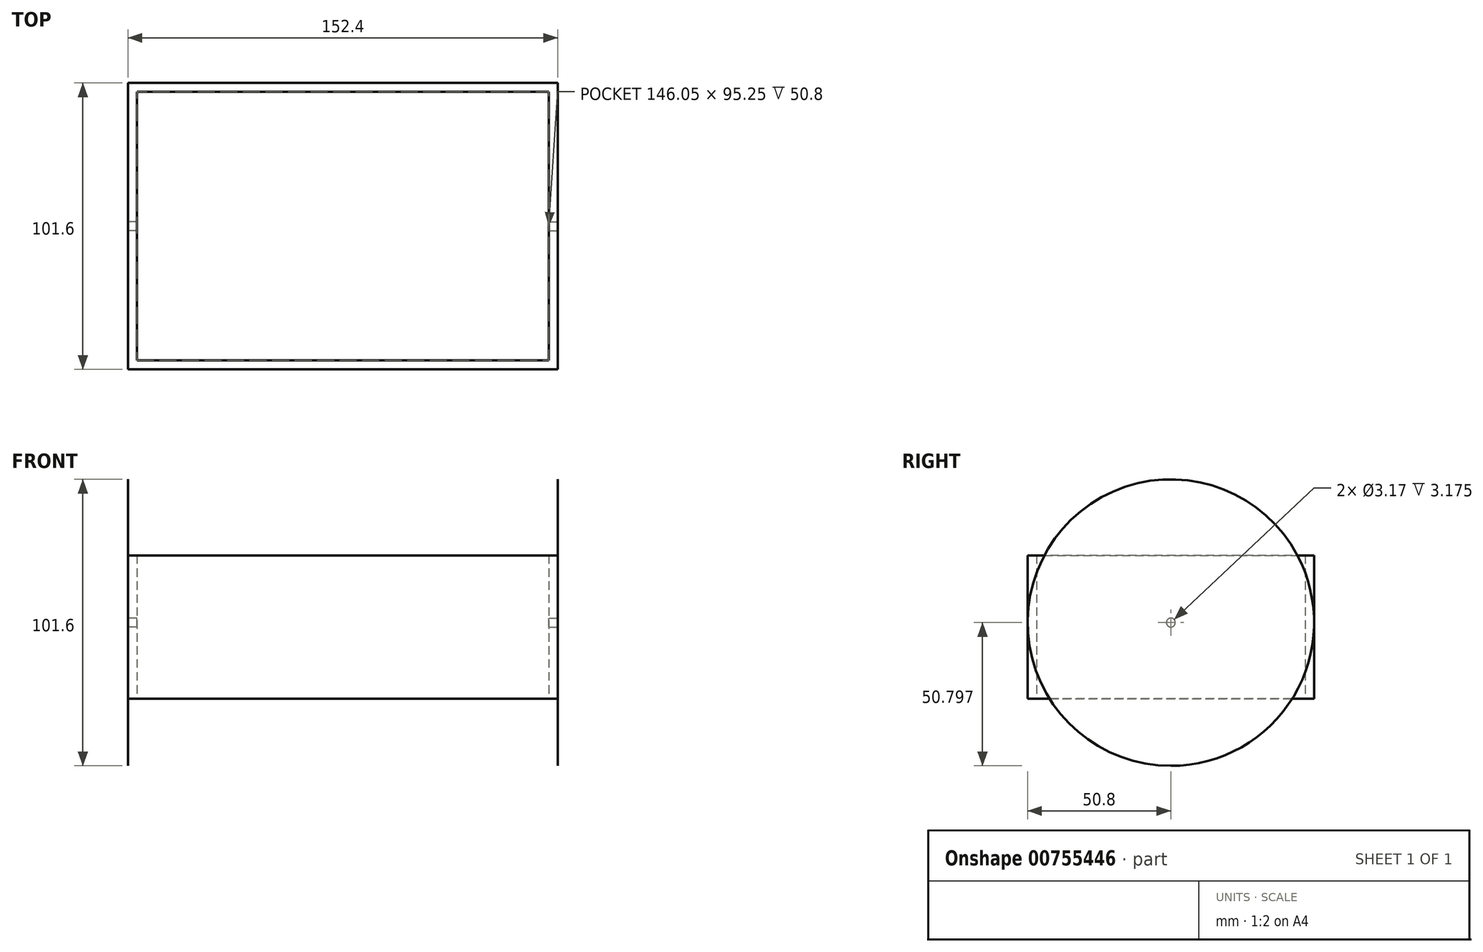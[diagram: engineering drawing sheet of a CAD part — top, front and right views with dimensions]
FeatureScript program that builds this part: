
annotation { "Feature Type Name" : "Feature", "Feature Type Description" : "" }
export const myFeature = defineFeature(function(context is Context, id is Id, definition is map)
    precondition{}
    {
        {
            var Q0;
            Q0=qCreatedBy(makeId("Top.planeOp"),FACE);
            var sketch = newSketch(context, id + "F0", { "sketchPlane" : qUnion([Q0])});
            skLineSegment(sketch, "E0.bottom", {"start": v(76.2, -50.8) * mm, "end": v(-76.2, -50.8) * mm});
            skLineSegment(sketch, "E0.top", {"start": v(76.2, 50.8) * mm, "end": v(-76.2, 50.8) * mm});
            skLineSegment(sketch, "E0.left", {"start": v(76.2, -50.8) * mm, "end": v(76.2, 50.8) * mm});
            skLineSegment(sketch, "E0.right", {"start": v(-76.2, -50.8) * mm, "end": v(-76.2, 50.8) * mm});
            skPoint(sketch, "E0.middle", {"position": v(0, 0) * mm});
            skSolve(sketch);
        }
        {
            var Q0;
            Q0 = qSketchRegion(id + "F0", true);
            extrude(context, id + "F1", {"entities" : qUnion([Q0]), "depth" : 1 / 203.2 * mm, "offsetDistance" : 25.4 * mm});
        }
        {
            var Q0;
            Q0=makeQuery(id+"F1.opExtrude","CAP_FACE",FACE,{"disambiguationData":[OSD([sQuery(id+"F0.wireOp",EDGE,"E0.bottom"),sQuery(id+"F0.wireOp",EDGE,"E0.top"),sQuery(id+"F0.wireOp",EDGE,"E0.left"),sQuery(id+"F0.wireOp",EDGE,"E0.right")])],"isStart":false});
            var sketch = newSketch(context, id + "F2", { "sketchPlane" : qUnion([Q0])});
            skLineSegment(sketch, "E1.bottom", {"start": v(-76.2, 50.8) * mm, "end": v(-73.03, 50.8) * mm});
            skLineSegment(sketch, "E1.top", {"start": v(-76.2, -50.8) * mm, "end": v(-73.03, -50.8) * mm});
            skLineSegment(sketch, "E1.left", {"start": v(-76.2, 50.8) * mm, "end": v(-76.2, -50.8) * mm});
            skLineSegment(sketch, "E1.right", {"start": v(-73.03, 50.8) * mm, "end": v(-73.03, -50.8) * mm});
            skLineSegment(sketch, "E2.bottom", {"start": v(76.2, 50.8) * mm, "end": v(73.02, 50.8) * mm});
            skLineSegment(sketch, "E2.top", {"start": v(76.2, -50.8) * mm, "end": v(73.03, -50.8) * mm});
            skLineSegment(sketch, "E2.left", {"start": v(76.2, 50.8) * mm, "end": v(76.2, -50.8) * mm});
            skLineSegment(sketch, "E2.right", {"start": v(73.02, 50.8) * mm, "end": v(73.03, -50.8) * mm});
            skLineSegment(sketch, "E3.bottom", {"start": v(-73.03, 50.8) * mm, "end": v(73.03, 50.8) * mm});
            skLineSegment(sketch, "E3.top", {"start": v(-73.03, 47.63) * mm, "end": v(73.03, 47.63) * mm});
            skLineSegment(sketch, "E3.left", {"start": v(-73.03, 50.8) * mm, "end": v(-73.03, 47.63) * mm});
            skLineSegment(sketch, "E3.right", {"start": v(73.03, 50.8) * mm, "end": v(73.03, 47.63) * mm});
            skLineSegment(sketch, "E4.bottom", {"start": v(-73.03, -50.8) * mm, "end": v(73.03, -50.8) * mm});
            skLineSegment(sketch, "E4.top", {"start": v(-73.03, -47.63) * mm, "end": v(73.03, -47.63) * mm});
            skLineSegment(sketch, "E4.left", {"start": v(-73.03, -50.8) * mm, "end": v(-73.03, -47.63) * mm});
            skLineSegment(sketch, "E4.right", {"start": v(73.03, -50.8) * mm, "end": v(73.03, -47.63) * mm});
            skSolve(sketch);
        }
        {
            var Q0;
            Q0 = qSketchRegion(id + "F2", true);
            extrude(context, id + "F3", {"entities" : qUnion([Q0]), "operationType" : NewBodyOperationType.ADD, "depth" : 50.8 * mm, "offsetDistance" : 25.4 * mm});
        }
        {
            var Q0;
            Q0=makeQuery(id+"F3.boolean.opBoolean","MERGE",FACE,{"derivedFrom":[makeQuery(id+"F1.opExtrude","SWEPT_FACE",FACE,{"disambiguationData":[OSD([sQuery(id+"F0.wireOp",EDGE,"E0.left")])]}),makeQuery(id+"F3.opExtrude","SWEPT_FACE",FACE,{"disambiguationData":[OSD([sQuery(id+"F2.wireOp",EDGE,"E2.left")])]})]});
            var sketch = newSketch(context, id + "F4", { "sketchPlane" : qUnion([Q0])});
            skLineSegment(sketch, "E5", {"start": v(-50.8, 26.99) * mm, "end": v(50.8, 26.99) * mm});
            skCircle(sketch, "E6", {"center": v(0, 26.99) * mm, "radius": 1.59 * mm});
            skSolve(sketch);
        }
        {
            var Q0;
            Q0 = qSketchRegion(id + "F4", true);
            extrude(context, id + "F5", {"entities" : qUnion([Q0]), "operationType" : NewBodyOperationType.REMOVE, "oppositeDirection" : true, "depth" : 25.4 * mm, "offsetDistance" : 25.4 * mm});
        }
        {
            var Q0;
            Q0=makeQuery(id+"F3.boolean.opBoolean","MERGE",FACE,{"derivedFrom":[makeQuery(id+"F1.opExtrude","SWEPT_FACE",FACE,{"disambiguationData":[OSD([sQuery(id+"F0.wireOp",EDGE,"E0.right")])]}),makeQuery(id+"F3.opExtrude","SWEPT_FACE",FACE,{"disambiguationData":[OSD([sQuery(id+"F2.wireOp",EDGE,"E1.left")])]})]});
            var sketch = newSketch(context, id + "F6", { "sketchPlane" : qUnion([Q0])});
            skCircle(sketch, "E7", {"center": v(0, 26.99) * mm, "radius": 1.59 * mm});
            skLineSegment(sketch, "E8", {"start": v(-50.8, 26.99) * mm, "end": v(50.8, 26.99) * mm});
            skSolve(sketch);
        }
        {
            var Q0;
            Q0 = qSketchRegion(id + "F6", true);
            extrude(context, id + "F7", {"entities" : qUnion([Q0]), "operationType" : NewBodyOperationType.REMOVE, "depth" : 1 / 203.2 * mm, "offsetDistance" : 25.4 * mm});
        }
        {
            var Q0;
            Q0 = qSketchRegion(id + "F6", true);
            extrude(context, id + "F8", {"entities" : qUnion([Q0]), "operationType" : NewBodyOperationType.REMOVE, "oppositeDirection" : true, "depth" : 25.4 * mm, "offsetDistance" : 25.4 * mm});
        }
        {
            var Q0;
            Q0=makeQuery(id+"F3.boolean.opBoolean","MERGE",FACE,{"derivedFrom":[makeQuery(id+"F1.opExtrude","SWEPT_FACE",FACE,{"disambiguationData":[OSD([sQuery(id+"F0.wireOp",EDGE,"E0.left")])]}),makeQuery(id+"F3.opExtrude","SWEPT_FACE",FACE,{"disambiguationData":[OSD([sQuery(id+"F2.wireOp",EDGE,"E2.left")])]})]});
            var sketch = newSketch(context, id + "F9", { "sketchPlane" : qUnion([Q0])});
            skCircle(sketch, "E9", {"center": v(0, 26.99) * mm, "radius": 50.8 * mm});
            skSolve(sketch);
        }
        {
            var Q0;
            Q0 = qSketchRegion(id + "F9", true);
            extrude(context, id + "F10", {"entities" : qUnion([Q0]), "operationType" : NewBodyOperationType.ADD, "depth" : 1 / 203.2 * mm, "offsetDistance" : 25.4 * mm});
        }
        {
            var Q0;
            Q0=makeQuery(id+"F3.boolean.opBoolean","MERGE",FACE,{"derivedFrom":[makeQuery(id+"F1.opExtrude","SWEPT_FACE",FACE,{"disambiguationData":[OSD([sQuery(id+"F0.wireOp",EDGE,"E0.right")])]}),makeQuery(id+"F3.opExtrude","SWEPT_FACE",FACE,{"disambiguationData":[OSD([sQuery(id+"F2.wireOp",EDGE,"E1.left")])]})]});
            var sketch = newSketch(context, id + "F11", { "sketchPlane" : qUnion([Q0])});
            skCircle(sketch, "E10", {"center": v(0, 26.99) * mm, "radius": 50.8 * mm});
            skSolve(sketch);
        }
        {
            var Q0;
            Q0 = qSketchRegion(id + "F11", true);
            extrude(context, id + "F12", {"entities" : qUnion([Q0]), "operationType" : NewBodyOperationType.ADD, "depth" : 1 / 203.2 * mm, "offsetDistance" : 25.4 * mm});
        }
    });
